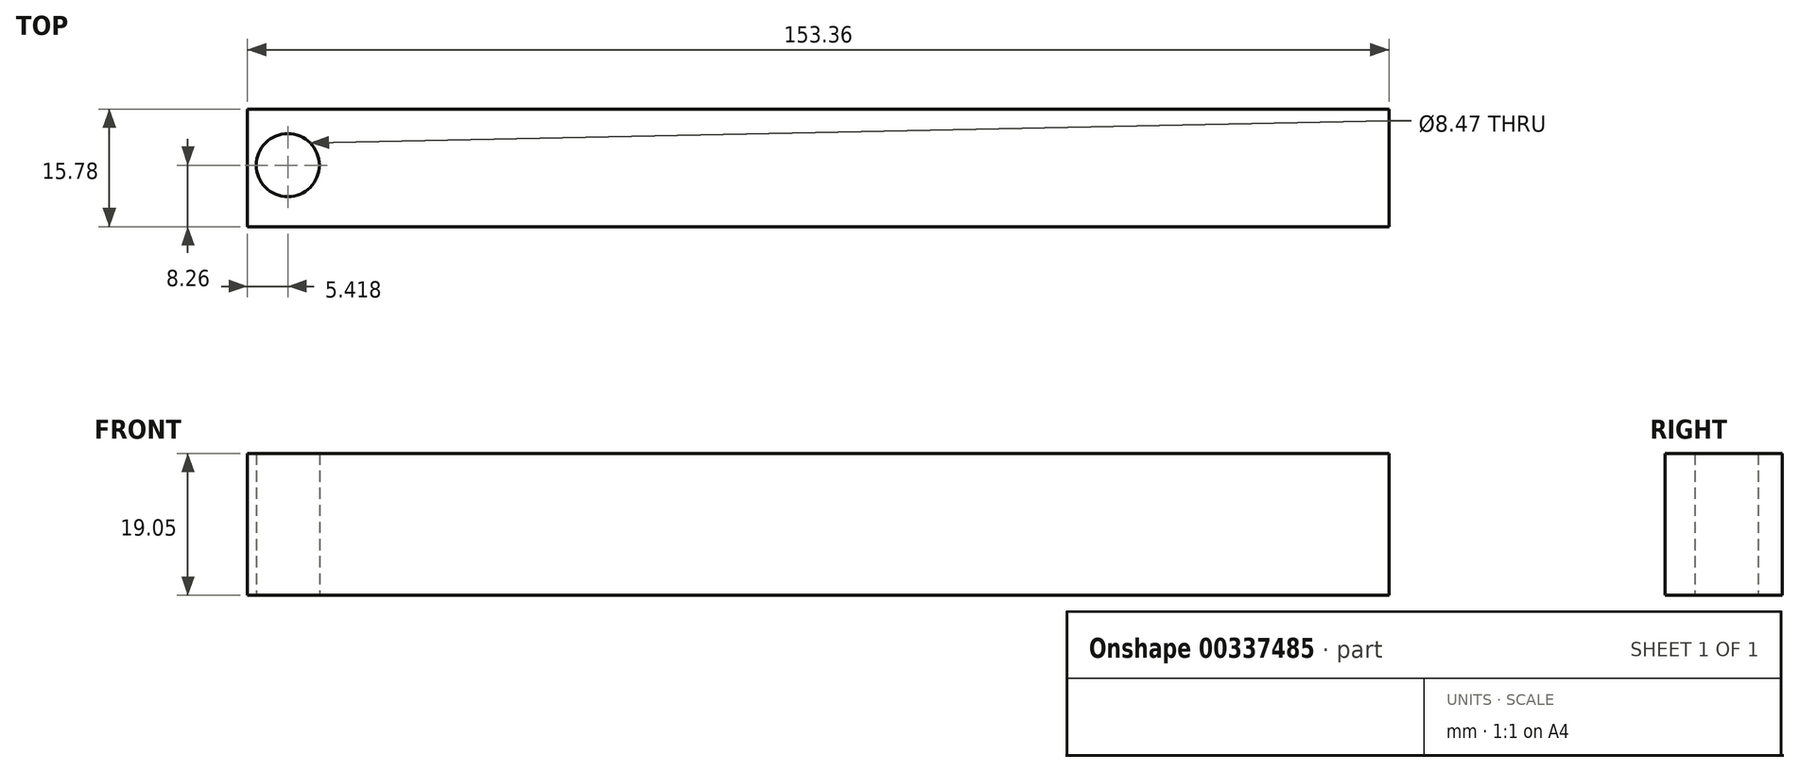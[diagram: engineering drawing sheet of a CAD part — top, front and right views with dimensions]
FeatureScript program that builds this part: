
annotation { "Feature Type Name" : "Feature", "Feature Type Description" : "" }
export const myFeature = defineFeature(function(context is Context, id is Id, definition is map)
    precondition{}
    {
        {
            var Q0;
            Q0=qCreatedBy(makeId("Top.planeOp"),FACE);
            var sketch = newSketch(context, id + "F0", { "sketchPlane" : qUnion([Q0])});
            skLineSegment(sketch, "E0.bottom", {"start": v(-54.5, 7.52) * mm, "end": v(98.87, 7.52) * mm});
            skLineSegment(sketch, "E0.top", {"start": v(-54.5, -8.26) * mm, "end": v(98.87, -8.26) * mm});
            skLineSegment(sketch, "E0.left", {"start": v(-54.5, 7.52) * mm, "end": v(-54.5, -8.26) * mm});
            skLineSegment(sketch, "E0.right", {"start": v(98.87, 7.52) * mm, "end": v(98.87, -8.26) * mm});
            skSolve(sketch);
        }
        {
            var Q0;
            Q0=makeQuery(id+"F0.imprint","IMPRINT",FACE,{"disambiguationData":[TD([[makeQuery(id+"F0.imprint","IMPRINT",EDGE,{"derivedFrom":sQuery(id+"F0.wireOp",EDGE,"E0.bottom")}),-1.0]])]});
            extrude(context, id + "F1", {"entities" : qUnion([Q0]), "depth" : 19.05 * mm});
        }
        {
            var Q0;
            Q0=qCreatedBy(makeId("Top.planeOp"),FACE);
            var sketch = newSketch(context, id + "F2", { "sketchPlane" : qUnion([Q0])});
            skCircle(sketch, "E1", {"center": v(-49.07, 0) * mm, "radius": 4.24 * mm});
            skSolve(sketch);
        }
        {
            var Q0;
            Q0=makeQuery(id+"F2.imprint","IMPRINT",FACE,{"disambiguationData":[TD([[makeQuery(id+"F2.imprint","IMPRINT",EDGE,{"derivedFrom":sQuery(id+"F2.wireOp",EDGE,"E1")}),1.0]])]});
            extrude(context, id + "F3", {"entities" : qUnion([Q0]), "operationType" : NewBodyOperationType.REMOVE, "depth" : 25.4 * mm});
        }
    });
